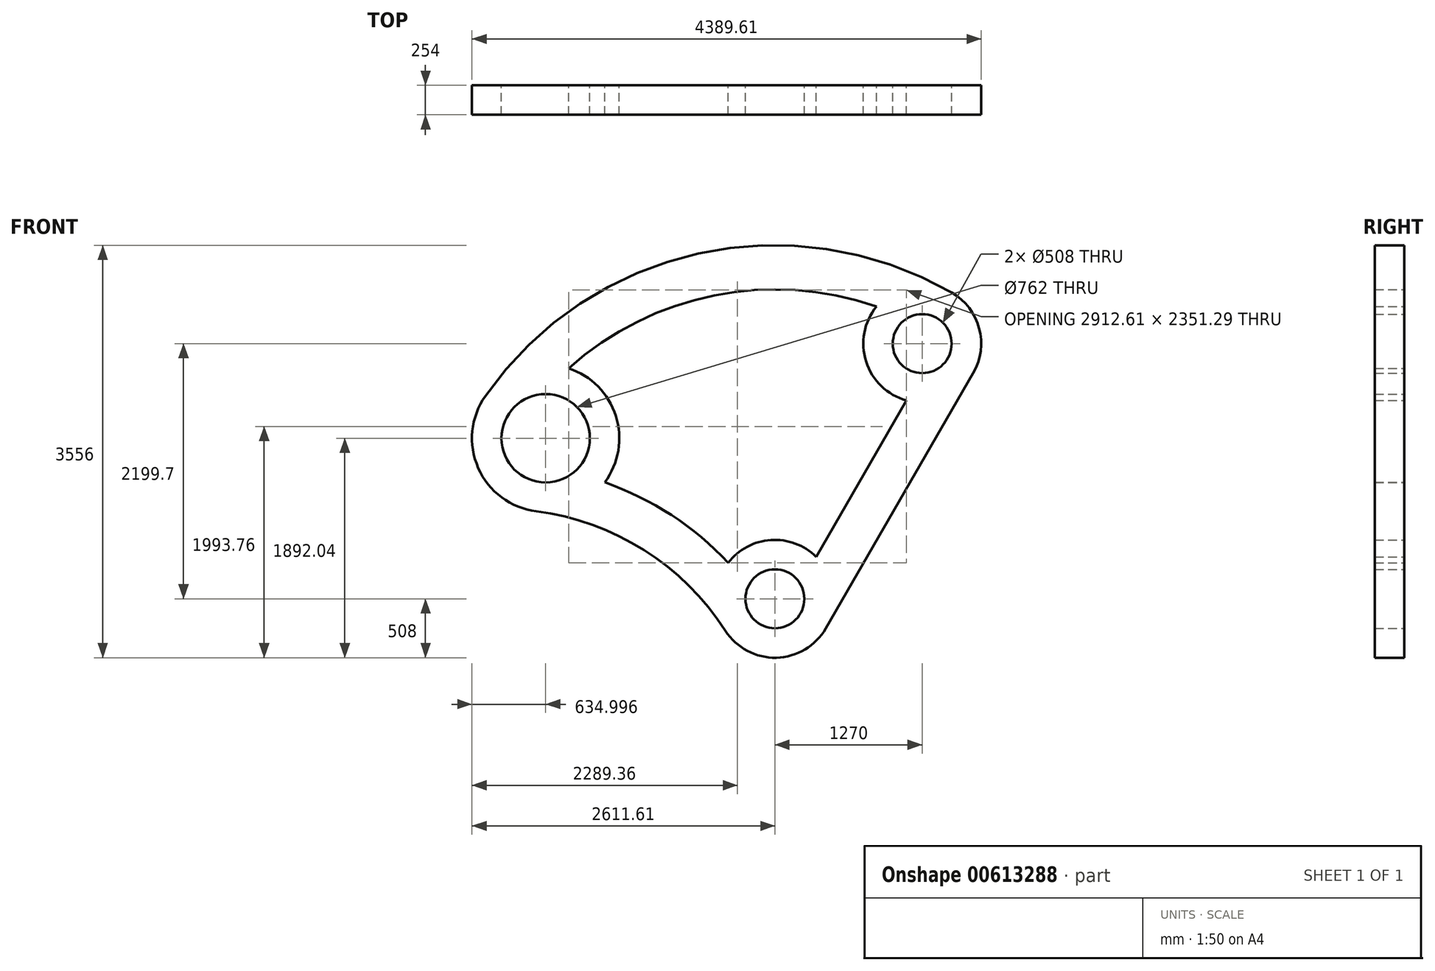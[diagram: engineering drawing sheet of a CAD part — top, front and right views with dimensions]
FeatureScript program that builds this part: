
annotation { "Feature Type Name" : "Feature", "Feature Type Description" : "" }
export const myFeature = defineFeature(function(context is Context, id is Id, definition is map)
    precondition{}
    {
        {
            var Q0;
            Q0=qCreatedBy(makeId("Front.planeOp"),FACE);
            var sketch = newSketch(context, id + "F0", { "sketchPlane" : qUnion([Q0])});
            skArc(sketch, "E0", {"start": v(1524, 2639.65) * mm, "mid": v(-659.7, 2975.75) * mm, "end": v(-2496.78, 1748.26) * mm});
            skLineSegment(sketch, "E1", {"start": v(355.92, 362.47) * mm, "end": v(1134.05, 1710.23) * mm});
            skArc(sketch, "E2", {"start": v(355.92, 362.47) * mm, "mid": v(-35, 506.8) * mm, "end": v(-402.36, 310.11) * mm});
            skCircle(sketch, "E3", {"center": v(0, 0) * mm, "radius": 254 * mm});
            skCircle(sketch, "E4", {"center": v(1270, 2199.7) * mm, "radius": 254 * mm});
            skArc(sketch, "E5", {"start": v(1709.94, 1945.7) * mm, "mid": v(1760.7, 2331.18) * mm, "end": v(1524, 2639.65) * mm});
            skArc(sketch, "E6", {"start": v(-2496.78, 1748.26) * mm, "mid": v(-2557.43, 1127.38) * mm, "end": v(-2057.52, 754.22) * mm});
            skCircle(sketch, "E7", {"center": v(-1976.61, 1384.04) * mm, "radius": 381 * mm});
            skLineSegment(sketch, "E8", {"start": v(1709.94, 1945.7) * mm, "end": v(439.94, -254) * mm});
            skArc(sketch, "E9.trimOffspring", {"start": v(875.15, 2519.33) * mm, "mid": v(-524.2, 2614.98) * mm, "end": v(-1778.56, 1987.36) * mm});
            skArc(sketch, "E10", {"start": v(-427.05, -275.12) * mm, "mid": v(-1128.45, 419.87) * mm, "end": v(-2057.52, 754.22) * mm});
            skArc(sketch, "E11.trimOffspring", {"start": v(-402.36, 310.11) * mm, "mid": v(-893.11, 721.55) * mm, "end": v(-1467.8, 1004.14) * mm});
            skArc(sketch, "E12.trimOffspring", {"start": v(-1467.8, 1004.14) * mm, "mid": v(-1371.14, 1575.41) * mm, "end": v(-1778.56, 1987.36) * mm});
            skArc(sketch, "E13.trimOffspring", {"start": v(875.15, 2519.33) * mm, "mid": v(786.17, 2044.88) * mm, "end": v(1134.05, 1710.23) * mm});
            skArc(sketch, "E14.trimOffspring", {"start": v(-427.05, -275.12) * mm, "mid": v(12.37, -507.85) * mm, "end": v(439.94, -254) * mm});
            skSolve(sketch);
        }
        {
            var Q0;
            Q0=makeQuery(id+"F0.imprint","IMPRINT",FACE,{"disambiguationData":[TD([[makeQuery(id+"F0.imprint","IMPRINT",EDGE,{"derivedFrom":sQuery(id+"F0.wireOp",EDGE,"E0")}),1.0]])]});
            extrude(context, id + "F1", {"entities" : qUnion([Q0]), "depth" : 254 * mm, "offsetDistance" : 25.4 * mm});
        }
    });
